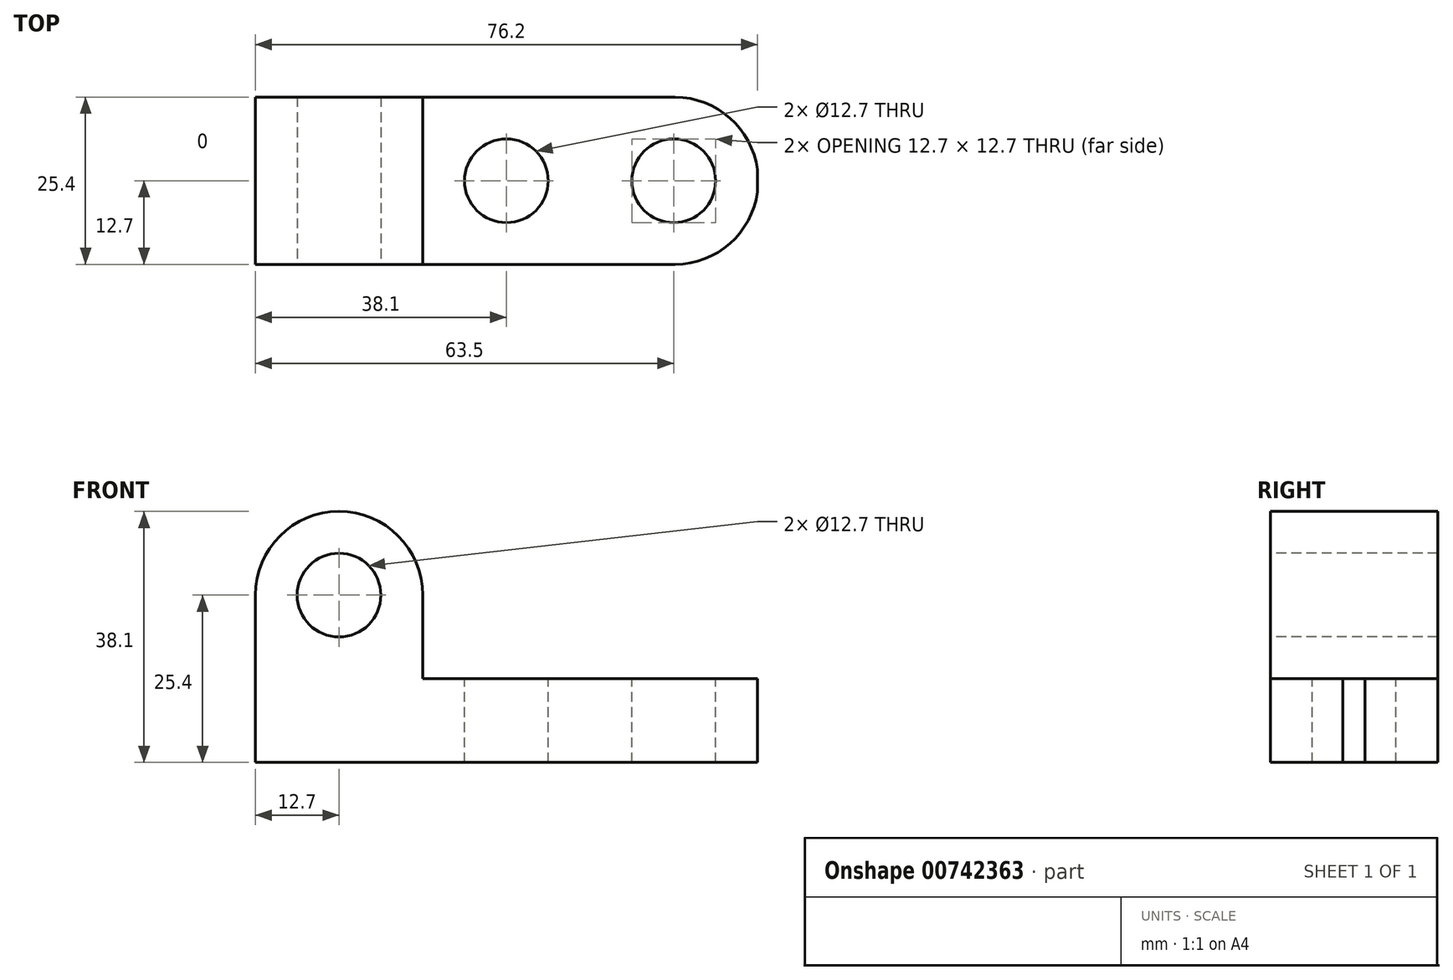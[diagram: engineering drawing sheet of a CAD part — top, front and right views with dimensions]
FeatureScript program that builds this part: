
annotation { "Feature Type Name" : "Feature", "Feature Type Description" : "" }
export const myFeature = defineFeature(function(context is Context, id is Id, definition is map)
    precondition{}
    {
        {
            var Q0;
            Q0=qCreatedBy(makeId("Front.planeOp"),FACE);
            var sketch = newSketch(context, id + "F0", { "sketchPlane" : qUnion([Q0])});
            skLineSegment(sketch, "E0", {"start": v(0, 38.1) * mm, "end": v(0, 0) * mm});
            skLineSegment(sketch, "E1", {"start": v(0, 0) * mm, "end": v(76.2, 0) * mm});
            skLineSegment(sketch, "E2", {"start": v(76.2, 0) * mm, "end": v(76.2, 12.7) * mm});
            skLineSegment(sketch, "E3", {"start": v(76.2, 12.7) * mm, "end": v(25.4, 12.7) * mm});
            skLineSegment(sketch, "E4", {"start": v(25.4, 12.7) * mm, "end": v(25.4, 38.1) * mm});
            skLineSegment(sketch, "E5", {"start": v(25.4, 38.1) * mm, "end": v(0, 38.1) * mm});
            skSolve(sketch);
        }
        {
            var Q0;
            Q0=makeQuery(id+"F0.imprint","IMPRINT",FACE,{"disambiguationData":[TD([[makeQuery(id+"F0.imprint","IMPRINT",EDGE,{"derivedFrom":sQuery(id+"F0.wireOp",EDGE,"E0")}),1.0]])]});
            extrude(context, id + "F1", {"entities" : qUnion([Q0]), "depth" : 25.4 * mm, "offsetDistance" : 25.4 * mm});
        }
        {
            var Q0;
            Q0=makeQuery(id+"F1.opExtrude","CAP_FACE",FACE,{"disambiguationData":[OSD([sQuery(id+"F0.wireOp",EDGE,"E0"),sQuery(id+"F0.wireOp",EDGE,"E1"),sQuery(id+"F0.wireOp",EDGE,"E2"),sQuery(id+"F0.wireOp",EDGE,"E3"),sQuery(id+"F0.wireOp",EDGE,"E4"),sQuery(id+"F0.wireOp",EDGE,"E5")])],"isStart":false});
            var sketch = newSketch(context, id + "F2", { "sketchPlane" : qUnion([Q0])});
            skCircle(sketch, "E6", {"center": v(12.7, 25.4) * mm, "radius": 6.35 * mm});
            skArc(sketch, "E7", {"start": v(25.4, 25.4) * mm, "mid": v(12.7, 38.1) * mm, "end": v(0, 25.4) * mm});
            skPoint(sketch, "E7.endSnap0", {"position": v(25.4, 25.4) * mm});
            skSolve(sketch);
        }
        {
            var Q0;
            {var subQ0=sQuery(id+"F2.wireOp",EDGE,"E7");var subQ1=makeQuery(id+"F1.opExtrude","CAP_EDGE",EDGE,{"disambiguationData":[OSD([sQuery(id+"F0.wireOp",EDGE,"E4")])],"isStart":false});var subQ2=makeQuery(id+"F2.imprint","INTERSECT",VERTEX,{"derivedFrom":[subQ1,subQ0]});Q0=makeQuery(id+"F2.imprint","IMPRINT",FACE,{"disambiguationData":[TD([[makeQuery(id+"F2.imprint","IMPRINT",EDGE,{"disambiguationData":[TD([[subQ2,-1.0]])],"derivedFrom":subQ0}),-1.0]])]});}
            var Q1;
            {var subQ0=sQuery(id+"F2.wireOp",EDGE,"E7");var subQ1=makeQuery(id+"F1.opExtrude","CAP_EDGE",EDGE,{"disambiguationData":[OSD([sQuery(id+"F0.wireOp",EDGE,"E0")])],"isStart":false});var subQ2=makeQuery(id+"F2.imprint","INTERSECT",VERTEX,{"derivedFrom":[subQ1,subQ0]});Q1=makeQuery(id+"F2.imprint","IMPRINT",FACE,{"disambiguationData":[TD([[makeQuery(id+"F2.imprint","IMPRINT",EDGE,{"disambiguationData":[TD([[subQ2,1.0]])],"derivedFrom":subQ0}),-1.0]])]});}
            var Q2;
            Q2=makeQuery(id+"F2.imprint","IMPRINT",FACE,{"disambiguationData":[TD([[makeQuery(id+"F2.imprint","IMPRINT",EDGE,{"derivedFrom":sQuery(id+"F2.wireOp",EDGE,"E6")}),1.0]])]});
            extrude(context, id + "F3", {"entities" : qUnion([Q0, Q1, Q2]), "operationType" : NewBodyOperationType.REMOVE, "endBound" : BoundingType.THROUGH_ALL, "oppositeDirection" : true, "depth" : 25.4 * mm, "offsetDistance" : 25.4 * mm});
        }
        {
            var Q0;
            Q0=makeQuery(id+"F1.opExtrude","SWEPT_FACE",FACE,{"disambiguationData":[OSD([sQuery(id+"F0.wireOp",EDGE,"E3")])]});
            var sketch = newSketch(context, id + "F4", { "sketchPlane" : qUnion([Q0])});
            skCircle(sketch, "E8", {"center": v(63.5, -12.7) * mm, "radius": 6.35 * mm});
            skCircle(sketch, "E9", {"center": v(38.1, -12.7) * mm, "radius": 6.35 * mm});
            skLineSegment(sketch, "E10", {"start": v(63.53, -6.35) * mm, "end": v(38.1, -6.35) * mm});
            skLineSegment(sketch, "E11", {"start": v(62.71, -19) * mm, "end": v(38.11, -19.05) * mm});
            skArc(sketch, "E12", {"start": v(63.53, -25.4) * mm, "mid": v(76.31, -12.7) * mm, "end": v(63.53, 0) * mm});
            skSolve(sketch);
        }
        {
            var Q0;
            {var subQ0=sQuery(id+"F4.wireOp",EDGE,"E10");Q0=makeQuery(id+"F4.imprint","IMPRINT",FACE,{"disambiguationData":[TD([[makeQuery(id+"F4.imprint","IMPRINT",EDGE,{"derivedFrom":subQ0}),1.0]])]});}
            var Q1;
            {var subQ0=sQuery(id+"F4.wireOp",EDGE,"E9");var subQ1=makeQuery(id+"F4.imprint","INTERSECT",VERTEX,{"derivedFrom":[subQ0,sQuery(id+"F4.wireOp",EDGE,"E10")]});Q1=makeQuery(id+"F4.imprint","IMPRINT",FACE,{"disambiguationData":[TD([[makeQuery(id+"F4.imprint","IMPRINT",EDGE,{"disambiguationData":[TD([[subQ1,-1.0]])],"derivedFrom":subQ0}),1.0]])]});}
            var Q2;
            {var subQ0=sQuery(id+"F4.wireOp",EDGE,"E8");var subQ2=makeQuery(id+"F4.imprint","IMPRINT",VERTEX,{"derivedFrom":subQ0});Q2=makeQuery(id+"F4.imprint","IMPRINT",FACE,{"disambiguationData":[TD([[makeQuery(id+"F4.imprint","IMPRINT",EDGE,{"disambiguationData":[TD([[subQ2,-1.0]])],"derivedFrom":subQ0}),1.0]])]});}
            var Q3;
            {var subQ0=sQuery(id+"F4.wireOp",EDGE,"E12");var subQ1=sQuery(id+"F0.wireOp",EDGE,"E3");var subQ2=makeQuery(id+"F1.opExtrude","CAP_EDGE",EDGE,{"disambiguationData":[OSD([subQ1])],"isStart":false});var subQ3=makeQuery(id+"F4.imprint","INTERSECT",VERTEX,{"disambiguationData":[OD(1.0)],"derivedFrom":[subQ2,subQ0]});Q3=makeQuery(id+"F4.imprint","IMPRINT",FACE,{"disambiguationData":[TD([[makeQuery(id+"F4.imprint","IMPRINT",EDGE,{"disambiguationData":[TD([[subQ3,-1.0]])],"derivedFrom":subQ0}),-1.0]])]});}
            var Q4;
            {var subQ0=sQuery(id+"F4.wireOp",EDGE,"E12");var subQ1=sQuery(id+"F0.wireOp",EDGE,"E3");var subQ4=makeQuery(id+"F1.opExtrude","CAP_EDGE",EDGE,{"disambiguationData":[OSD([subQ1])],"isStart":true});var subQ5=makeQuery(id+"F4.imprint","INTERSECT",VERTEX,{"disambiguationData":[OD(1.0)],"derivedFrom":[subQ4,subQ0]});Q4=makeQuery(id+"F4.imprint","IMPRINT",FACE,{"disambiguationData":[TD([[makeQuery(id+"F4.imprint","IMPRINT",EDGE,{"disambiguationData":[TD([[subQ5,1.0]])],"derivedFrom":subQ0}),-1.0]])]});}
            extrude(context, id + "F5", {"entities" : qUnion([Q0, Q1, Q2, Q3, Q4]), "operationType" : NewBodyOperationType.REMOVE, "endBound" : BoundingType.THROUGH_ALL, "oppositeDirection" : true, "depth" : 25.4 * mm, "offsetDistance" : 25.4 * mm});
        }
    });
